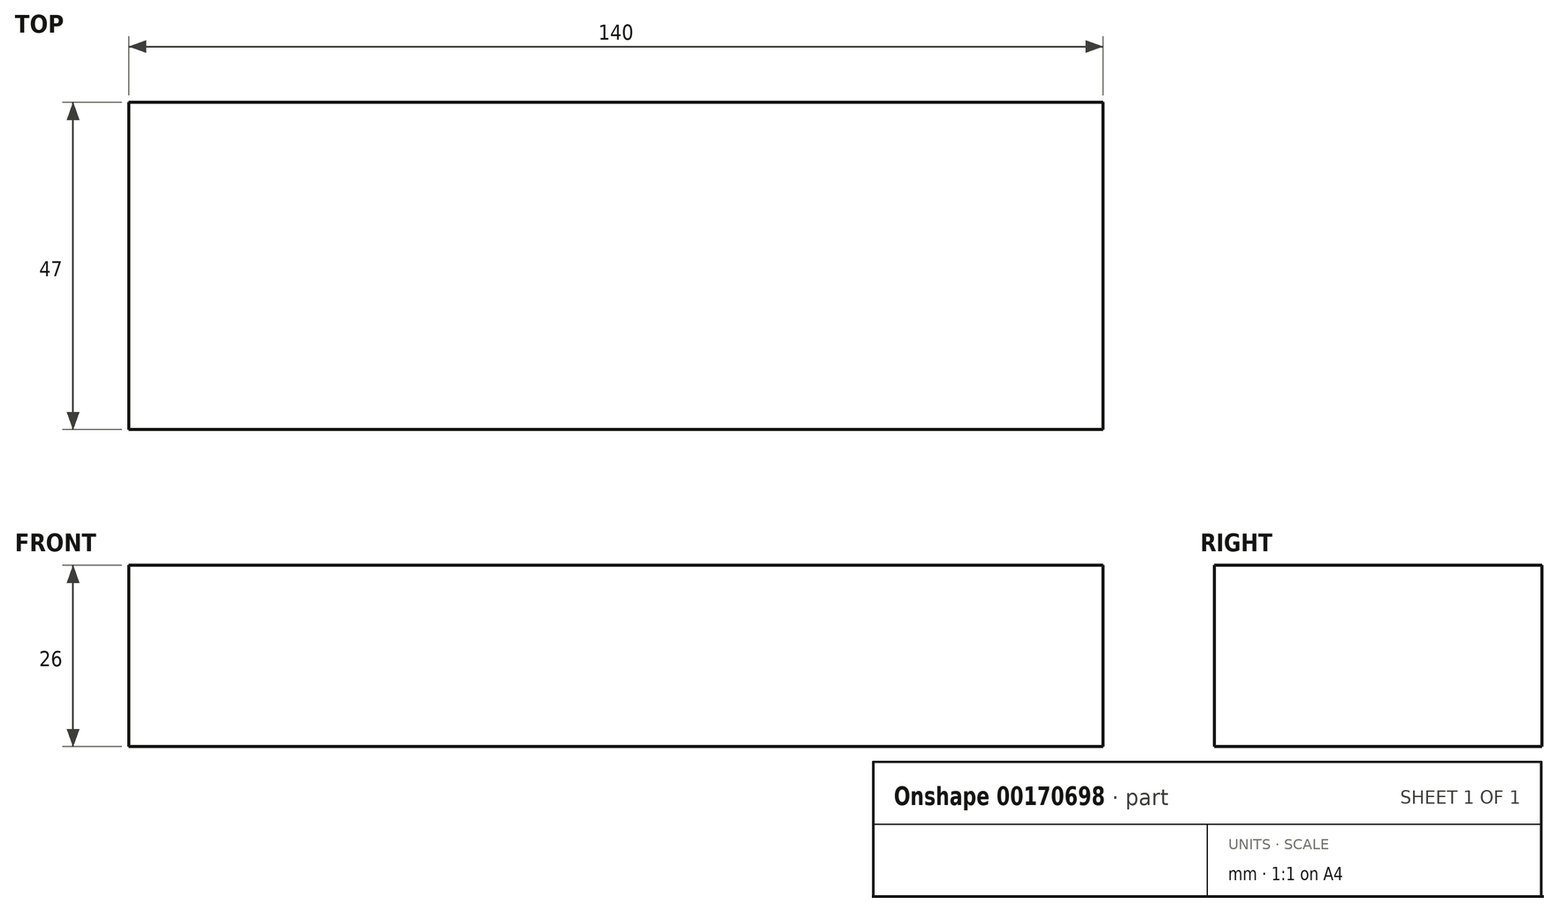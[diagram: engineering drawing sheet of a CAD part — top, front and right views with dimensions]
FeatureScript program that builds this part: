
annotation { "Feature Type Name" : "Feature", "Feature Type Description" : "" }
export const myFeature = defineFeature(function(context is Context, id is Id, definition is map)
    precondition{}
    {
        {
            var Q0;
            Q0=qCreatedBy(makeId("Top.planeOp"),FACE);
            var sketch = newSketch(context, id + "F0", { "sketchPlane" : qUnion([Q0])});
            skLineSegment(sketch, "E0.bottom", {"start": v(0, 0) * mm, "end": v(140, 0) * mm});
            skLineSegment(sketch, "E0.top", {"start": v(0, 47) * mm, "end": v(140, 47) * mm});
            skLineSegment(sketch, "E0.left", {"start": v(0, 0) * mm, "end": v(0, 47) * mm});
            skLineSegment(sketch, "E0.right", {"start": v(140, 0) * mm, "end": v(140, 47) * mm});
            skSolve(sketch);
        }
        {
            var Q0;
            Q0=makeQuery(id+"F0.imprint","IMPRINT",FACE,{"disambiguationData":[TD([[makeQuery(id+"F0.imprint","IMPRINT",EDGE,{"derivedFrom":sQuery(id+"F0.wireOp",EDGE,"E0.bottom")}),1.0]])]});
            extrude(context, id + "F1", {"entities" : qUnion([Q0]), "depth" : 26 * mm});
        }
    });
